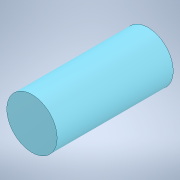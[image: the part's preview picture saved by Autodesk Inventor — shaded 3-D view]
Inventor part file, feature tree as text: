
AUTODESK INVENTOR PART (.ipt)
format: ipt  version: 2022 (Build 260153000, 153)  size: 100,864 bytes
history: native  units: in
note: dims shown in document units (in); Inventor stores cm internally (conversion verified against a paired STEP export)
features: extrude x1, sketch x1
ambient origin geometry x8: Origin, YZ Plane, XZ Plane, XY Plane, X Axis, Y Axis, Z Axis, Center Point
bodies: Solid1 (feature_tree)
feature tree (2):
  extrude  "Extrusion1"  Depth=0.5906in
  sketch  "Sketch2"  dims[d0=0.2559in d1=0.5906in d2=0.0in]
